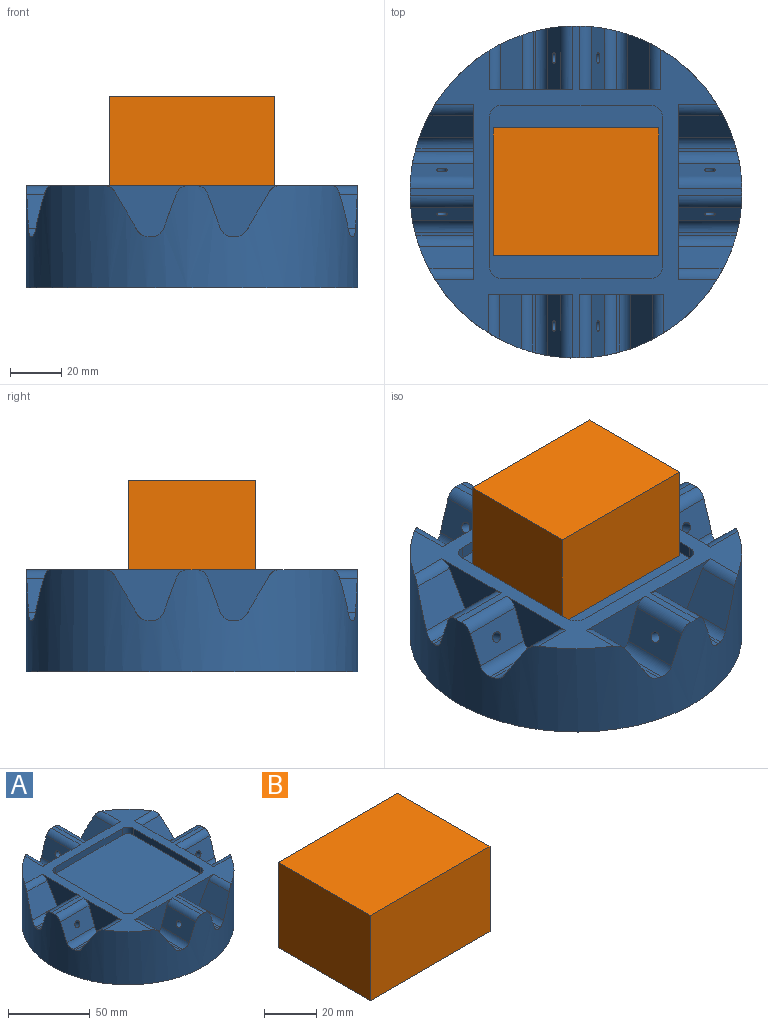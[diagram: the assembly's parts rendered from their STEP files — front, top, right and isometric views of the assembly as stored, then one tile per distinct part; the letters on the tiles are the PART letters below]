
ASSEMBLY  parts=2 mates=1
PART A: 100 faces, bbox 130x130x40 mm
  f0: plane 130x130mm, normal (0,0,1), area 2984.8mm2, adj f14,f15,f16,f20,f24,f28,f32,f33
  f1: plane 24.74x13.45mm, normal (0.94,0,0.34), area 334.7mm2, adj f14,f34,f69,f70,f95
  f2: plane 23.06x1.33mm, normal (0,0,1), area 30.5mm2, adj f14,f34,f70,f71
  f3: plane 21.36x15mm, normal (-0.87,0,0.5), area 339.6mm2, adj f14,f34,f68,f71
  f4: plane 23.06x1.33mm, normal (0,0,1), area 30.5mm2, adj f16,f34,f64,f65
  f5: plane 24.74x13.45mm, normal (0,-0.94,0.34), area 334.7mm2, adj f16,f34,f65,f66,f88
  f6: plane 21.36x15mm, normal (0,0.87,0.5), area 339.6mm2, adj f16,f34,f64,f67
  f7: plane 21.36x15mm, normal (0.87,0,0.5), area 339.6mm2, adj f15,f34,f73,f74
  f8: plane 23.06x1.33mm, normal (0,0,1), area 30.5mm2, adj f15,f34,f74,f75
  f9: plane 24.74x13.45mm, normal (-0.94,0,0.34), area 334.7mm2, adj f15,f34,f72,f75,f94
  f10: plane 21.36x15mm, normal (0,0.87,0.5), area 339.6mm2, adj f33,f34,f44,f45
  f11: plane 24.74x13.45mm, normal (0,-0.94,0.34), area 334.7mm2, adj f33,f34,f46,f47,f77
  f12: plane 23.06x1.33mm, normal (0,0,1), area 30.5mm2, adj f33,f34,f44,f47
  f13: plane 130x130mm, normal (0,0,-1), area 13273.2mm2, adj f34
  f14: plane 32.93x20mm, normal (0,-1,0), area 342.7mm2, adj f0,f1,f2,f3,f68,f69,f70,f71
  f15: plane 32.93x20mm, normal (0,-1,0), area 342.7mm2, adj f0,f7,f8,f9,f72,f73,f74,f75
  f16: plane 32.93x20mm, normal (1,0,0), area 342.7mm2, adj f0,f4,f5,f6,f64,f65,f66,f67
  f17: plane 21.36x15mm, normal (0,-0.87,0.5), area 339.6mm2, adj f20,f34,f60,f61
  f18: plane 24.74x13.45mm, normal (0,0.94,0.34), area 334.7mm2, adj f20,f34,f62,f63,f89
  f19: plane 23.06x1.33mm, normal (0,0,1), area 30.5mm2, adj f20,f34,f60,f63
  f20: plane 32.93x20mm, normal (1,0,0), area 342.7mm2, adj f0,f17,f18,f19,f60,f61,f62,f63
  f21: plane 21.77x15mm, normal (-0.87,0,0.5), area 348.4mm2, adj f24,f34,f57,f58
  f22: plane 23.06x0.14mm, normal (0,0,1), area 3.1mm2, adj f24,f34,f58,f59
  f23: plane 24.74x13.45mm, normal (0.94,0,0.34), area 334.7mm2, adj f24,f34,f56,f59,f82
  f24: plane 31.74x20mm, normal (0,1,0), area 318.7mm2, adj f0,f21,f22,f23,f56,f57,f58,f59
  f25: plane 21.49x15mm, normal (0.87,0,0.5), area 342.4mm2, adj f28,f34,f52,f53
  f26: plane 24.74x13.45mm, normal (-0.94,0,0.34), area 334.7mm2, adj f28,f34,f54,f55,f83
  f27: plane 23.06x0.96mm, normal (0,0,1), area 22mm2, adj f28,f34,f52,f55
  f28: plane 32.56x20mm, normal (0,1,0), area 335.2mm2, adj f0,f25,f26,f27,f52,f53,f54,f55
  f29: plane 21.36x15mm, normal (0,-0.87,0.5), area 339.6mm2, adj f32,f34,f49,f50
  f30: plane 23.06x1.33mm, normal (0,0,1), area 30.5mm2, adj f32,f34,f50,f51
  f31: plane 24.74x13.45mm, normal (0,0.94,0.34), area 334.7mm2, adj f32,f34,f48,f51,f76
  f32: plane 32.93x20mm, normal (-1,0,0), area 342.7mm2, adj f0,f29,f30,f31,f48,f49,f50,f51
  f33: plane 32.93x20mm, normal (-1,0,0), area 342.7mm2, adj f0,f10,f11,f12,f44,f45,f46,f47
  f34: cylinder r=65mm len=130mm, axis (0,0,1), area 13510.1mm2, adj f0,f1,f2,f3,f4,f5,f6,f7
  f35: plane 58x5mm, normal (1,0,0), area 290mm2, adj f0,f39,f40,f41
  f36: plane 58x5mm, normal (0,1,0), area 290mm2, adj f0,f39,f41,f42
  f37: plane 58x5mm, normal (-1,0,0), area 290mm2, adj f0,f39,f42,f43
  f38: plane 58x5mm, normal (0,-1,0), area 290mm2, adj f0,f39,f40,f43
  f39: plane 68x68mm, normal (0,0,1), area 4602.5mm2, adj f35,f36,f37,f38,f40,f41,f42,f43
  f40: cylinder r=5mm len=5mm, axis (0,0,-1), area 39.3mm2, adj f0,f35,f38,f39
  f41: cylinder r=5mm len=5mm, axis (0,0,1), area 39.3mm2, adj f0,f35,f36,f39
  f42: cylinder r=5mm len=5mm, axis (0,0,-1), area 39.3mm2, adj f0,f36,f37,f39
  f43: cylinder r=5mm len=5mm, axis (0,0,1), area 39.3mm2, adj f0,f37,f38,f39
  f44: cylinder r=5mm len=22.71mm, axis (1,0,0), area 115.1mm2, adj f10,f12,f33,f34
  f45: cylinder r=5mm len=17.61mm, axis (1,0,0), area 86.6mm2, adj f0,f10,f33,f34
  f46: cylinder r=5mm len=24.98mm, axis (1,0,0), area 151.8mm2, adj f0,f11,f33,f34
  f47: cylinder r=5mm len=24.05mm, axis (1,0,0), area 144.5mm2, adj f11,f12,f33,f34
  f48: cylinder r=5mm len=24.98mm, axis (-1,0,0), area 151.8mm2, adj f0,f31,f32,f34
  f49: cylinder r=5mm len=17.61mm, axis (-1,0,0), area 86.6mm2, adj f0,f29,f32,f34
  f50: cylinder r=5mm len=22.71mm, axis (1,0,0), area 115.1mm2, adj f29,f30,f32,f34
  f51: cylinder r=5mm len=24.05mm, axis (1,0,0), area 144.5mm2, adj f30,f31,f32,f34
  f52: cylinder r=5mm len=22.81mm, axis (0,-1,0), area 115.8mm2, adj f25,f27,f28,f34
  f53: cylinder r=5mm len=17.8mm, axis (0,-1,0), area 87.7mm2, adj f0,f25,f28,f34
  f54: cylinder r=5mm len=24.98mm, axis (0,-1,0), area 151.8mm2, adj f0,f26,f28,f34
  f55: cylinder r=5mm len=24.05mm, axis (0,-1,0), area 144.5mm2, adj f26,f27,f28,f34
  f56: cylinder r=5mm len=24.98mm, axis (0,1,0), area 151.8mm2, adj f0,f23,f24,f34
  f57: cylinder r=5mm len=18.22mm, axis (0,1,0), area 90mm2, adj f0,f21,f24,f34
  f58: cylinder r=5mm len=23.02mm, axis (0,-1,0), area 117.1mm2, adj f21,f22,f24,f34
  f59: cylinder r=5mm len=24.05mm, axis (0,-1,0), area 144.5mm2, adj f22,f23,f24,f34
  f60: cylinder r=5mm len=22.71mm, axis (-1,0,0), area 115.1mm2, adj f17,f19,f20,f34
  f61: cylinder r=5mm len=17.61mm, axis (-1,0,0), area 86.6mm2, adj f0,f17,f20,f34
  f62: cylinder r=5mm len=24.98mm, axis (-1,0,0), area 151.8mm2, adj f0,f18,f20,f34
  f63: cylinder r=5mm len=24.05mm, axis (-1,0,0), area 144.5mm2, adj f18,f19,f20,f34
  f64: cylinder r=5mm len=22.71mm, axis (-1,0,0), area 115.1mm2, adj f4,f6,f16,f34
  f65: cylinder r=5mm len=24.05mm, axis (-1,0,0), area 144.5mm2, adj f4,f5,f16,f34
  f66: cylinder r=5mm len=24.98mm, axis (1,0,0), area 151.8mm2, adj f0,f5,f16,f34
  f67: cylinder r=5mm len=17.61mm, axis (1,0,0), area 86.6mm2, adj f0,f6,f16,f34
  f68: cylinder r=5mm len=17.61mm, axis (0,1,0), area 86.6mm2, adj f0,f3,f14,f34
  f69: cylinder r=5mm len=24.98mm, axis (0,1,0), area 151.8mm2, adj f0,f1,f14,f34
  f70: cylinder r=5mm len=24.05mm, axis (0,1,0), area 144.5mm2, adj f1,f2,f14,f34
  f71: cylinder r=5mm len=22.71mm, axis (0,1,0), area 115.1mm2, adj f2,f3,f14,f34
  f72: cylinder r=5mm len=24.98mm, axis (0,-1,0), area 151.8mm2, adj f0,f9,f15,f34
  f73: cylinder r=5mm len=17.61mm, axis (0,-1,0), area 86.6mm2, adj f0,f7,f15,f34
  f74: cylinder r=5mm len=22.71mm, axis (0,1,0), area 115.1mm2, adj f7,f8,f15,f34
  f75: cylinder r=5mm len=24.05mm, axis (0,1,0), area 144.5mm2, adj f8,f9,f15,f34
  f76: cylinder r=2.1mm len=10.64mm, axis (0,0.94,0.34), area 117.8mm2, adj f31,f77,f78,f79
  f77: cylinder r=2.1mm len=10.63mm, axis (0,-0.94,0.34), area 117.8mm2, adj f11,f76,f80,f81
  f78: cylinder r=2.1mm len=4.2mm, axis (0,-0.94,0.34), area 2.7mm2, adj f76,f79,f81
  f79: plane 4.2x2.27mm, normal (0,-0.94,0.34), area 0.9mm2, adj f76,f78
  f80: plane 4.2x2.27mm, normal (0,0.94,0.34), area 0.9mm2, adj f77,f81
  f81: cylinder r=2.1mm len=4.2mm, axis (0,0.94,0.34), area 2.7mm2, adj f77,f78,f80
  f82: cylinder r=2.1mm len=10.63mm, axis (0.94,0,0.34), area 117.8mm2, adj f23,f83,f84,f85
  f83: cylinder r=2.1mm len=10.64mm, axis (-0.94,0,0.34), area 117.8mm2, adj f26,f82,f86,f87
  f84: cylinder r=2.1mm len=4.2mm, axis (-0.94,0,0.34), area 2.7mm2, adj f82,f85,f87
  f85: plane 4.2x2.27mm, normal (-0.94,0,0.34), area 0.9mm2, adj f82,f84
  f86: plane 4.2x2.27mm, normal (0.94,0,0.34), area 0.9mm2, adj f83,f87
  f87: cylinder r=2.1mm len=4.2mm, axis (0.94,0,0.34), area 2.7mm2, adj f83,f84,f86
  f88: cylinder r=2.1mm len=10.63mm, axis (0,-0.94,0.34), area 117.8mm2, adj f5,f89,f90,f91
  f89: cylinder r=2.1mm len=10.64mm, axis (0,0.94,0.34), area 117.8mm2, adj f18,f88,f92,f93
  f90: cylinder r=2.1mm len=4.2mm, axis (0,0.94,0.34), area 2.7mm2, adj f88,f91,f93
  f91: plane 4.2x2.27mm, normal (0,0.94,0.34), area 0.9mm2, adj f88,f90
  f92: plane 4.2x2.27mm, normal (0,-0.94,0.34), area 0.9mm2, adj f89,f93
  f93: cylinder r=2.1mm len=4.2mm, axis (0,-0.94,0.34), area 2.7mm2, adj f89,f90,f92
  f94: cylinder r=2.1mm len=10.64mm, axis (-0.94,0,0.34), area 117.8mm2, adj f9,f95,f96,f97
  f95: cylinder r=2.1mm len=10.63mm, axis (0.94,0,0.34), area 117.8mm2, adj f1,f94,f98,f99
  f96: cylinder r=2.1mm len=4.2mm, axis (0.94,0,0.34), area 2.7mm2, adj f94,f97,f99
  f97: plane 4.2x2.27mm, normal (0.94,0,0.34), area 0.9mm2, adj f94,f96
  f98: plane 4.2x2.27mm, normal (-0.94,0,0.34), area 0.9mm2, adj f95,f99
  f99: cylinder r=2.1mm len=4.2mm, axis (-0.94,0,0.34), area 2.7mm2, adj f95,f96,f98
PART B: 6 faces, bbox 65x50x40 mm
  f0: plane 50x40mm, normal (-1,0,0), area 2000mm2, adj f1,f3,f4,f5
  f1: plane 65x40mm, normal (0,-1,0), area 2600mm2, adj f0,f2,f4,f5
  f2: plane 50x40mm, normal (1,0,0), area 2000mm2, adj f1,f3,f4,f5
  f3: plane 65x40mm, normal (0,1,0), area 2600mm2, adj f0,f2,f4,f5
  f4: plane 65x50mm, normal (0,0,1), area 3250mm2, adj f0,f1,f2,f3
  f5: plane 65x50mm, normal (0,0,-1), area 3250mm2, adj f0,f1,f2,f3
PLACE A t=(-13.8,1.38,-5.98)mm
PLACE B rot(axis=(1,0,0),180deg) t=(-13.8,1.38,69.02)mm
MATE fastened B.f4 <-> A.f34  axis (0,0,-1) through (-13.8,1.38,29.02)mm
